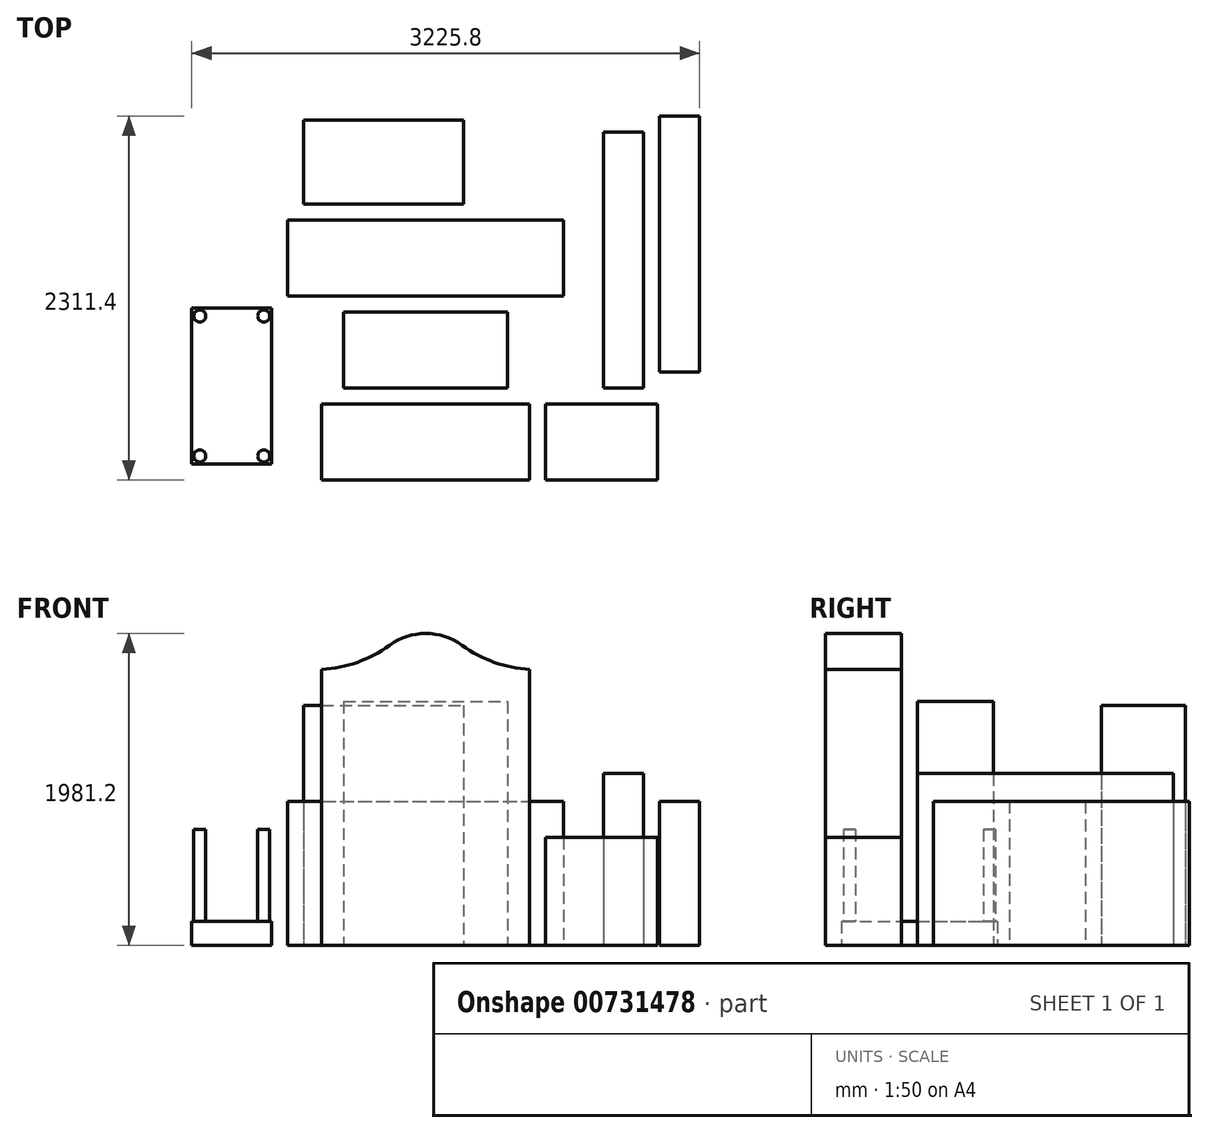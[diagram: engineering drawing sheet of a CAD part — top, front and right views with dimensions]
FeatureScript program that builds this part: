
annotation { "Feature Type Name" : "Feature", "Feature Type Description" : "" }
export const myFeature = defineFeature(function(context is Context, id is Id, definition is map)
    precondition{}
    {
        {
            var Q0;
            Q0=qCreatedBy(makeId("Top.planeOp"),FACE);
            var sketch = newSketch(context, id + "F0", { "sketchPlane" : qUnion([Q0])});
            skLineSegment(sketch, "E0.bottom", {"start": v(-876.3, 482.6) * mm, "end": v(876.3, 482.6) * mm});
            skLineSegment(sketch, "E0.top", {"start": v(-876.3, 0) * mm, "end": v(876.3, 0) * mm});
            skLineSegment(sketch, "E0.left", {"start": v(-876.3, 482.6) * mm, "end": v(-876.3, 0) * mm});
            skLineSegment(sketch, "E0.right", {"start": v(876.3, 482.6) * mm, "end": v(876.3, 0) * mm});
            skLineSegment(sketch, "E1.bottom", {"start": v(-520.7, -101.6) * mm, "end": v(520.7, -101.6) * mm});
            skLineSegment(sketch, "E1.top", {"start": v(-520.7, -584.2) * mm, "end": v(520.7, -584.2) * mm});
            skLineSegment(sketch, "E1.left", {"start": v(-520.7, -101.6) * mm, "end": v(-520.7, -584.2) * mm});
            skLineSegment(sketch, "E1.right", {"start": v(520.7, -101.6) * mm, "end": v(520.7, -584.2) * mm});
            skLineSegment(sketch, "E2.bottom", {"start": v(-660.4, -685.8) * mm, "end": v(660.4, -685.8) * mm});
            skLineSegment(sketch, "E2.top", {"start": v(-660.4, -1168.4) * mm, "end": v(660.4, -1168.4) * mm});
            skLineSegment(sketch, "E2.left", {"start": v(-660.4, -685.8) * mm, "end": v(-660.4, -1168.4) * mm});
            skLineSegment(sketch, "E2.right", {"start": v(660.4, -685.8) * mm, "end": v(660.4, -1168.4) * mm});
            skLineSegment(sketch, "E3", {"start": v(0, -101.6) * mm, "end": v(0, 0) * mm});
            skLineSegment(sketch, "E4", {"start": v(0, -584.2) * mm, "end": v(0, -685.8) * mm});
            skLineSegment(sketch, "E5.bottom", {"start": v(-774.7, 584.2) * mm, "end": v(241.3, 584.2) * mm});
            skLineSegment(sketch, "E5.top", {"start": v(-774.7, 1117.6) * mm, "end": v(241.3, 1117.6) * mm});
            skLineSegment(sketch, "E5.left", {"start": v(-774.7, 584.2) * mm, "end": v(-774.7, 1117.6) * mm});
            skLineSegment(sketch, "E5.right", {"start": v(241.3, 584.2) * mm, "end": v(241.3, 1117.6) * mm});
            skLineSegment(sketch, "E6.bottom", {"start": v(762, -1168.4) * mm, "end": v(1473.2, -1168.4) * mm});
            skLineSegment(sketch, "E6.top", {"start": v(762, -685.8) * mm, "end": v(1473.2, -685.8) * mm});
            skLineSegment(sketch, "E6.left", {"start": v(762, -1168.4) * mm, "end": v(762, -685.8) * mm});
            skLineSegment(sketch, "E6.right", {"start": v(1473.2, -1168.4) * mm, "end": v(1473.2, -685.8) * mm});
            skLineSegment(sketch, "E7.bottom", {"start": v(1130.3, -584.2) * mm, "end": v(1384.3, -584.2) * mm});
            skLineSegment(sketch, "E7.top", {"start": v(1130.3, 1041.4) * mm, "end": v(1384.3, 1041.4) * mm});
            skLineSegment(sketch, "E7.left", {"start": v(1130.3, -584.2) * mm, "end": v(1130.3, 1041.4) * mm});
            skLineSegment(sketch, "E7.right", {"start": v(1384.3, -584.2) * mm, "end": v(1384.3, 1041.4) * mm});
            skLineSegment(sketch, "E8.bottom", {"start": v(1485.9, 1143) * mm, "end": v(1739.9, 1143) * mm});
            skLineSegment(sketch, "E8.top", {"start": v(1485.9, -482.6) * mm, "end": v(1739.9, -482.6) * mm});
            skLineSegment(sketch, "E8.left", {"start": v(1485.9, 1143) * mm, "end": v(1485.9, -482.6) * mm});
            skLineSegment(sketch, "E8.right", {"start": v(1739.9, 1143) * mm, "end": v(1739.9, -482.6) * mm});
            skLineSegment(sketch, "E9.bottom", {"start": v(-977.9, -1066.8) * mm, "end": v(-1485.9, -1066.8) * mm});
            skLineSegment(sketch, "E9.top", {"start": v(-977.9, -76.2) * mm, "end": v(-1485.9, -76.2) * mm});
            skLineSegment(sketch, "E9.left", {"start": v(-977.9, -1066.8) * mm, "end": v(-977.9, -76.2) * mm});
            skLineSegment(sketch, "E9.right", {"start": v(-1485.9, -1066.8) * mm, "end": v(-1485.9, -76.2) * mm});
            skLineSegment(sketch, "E10.0", {"start": v(-1028.7, -127) * mm, "end": v(-1435.1, -127) * mm});
            skLineSegment(sketch, "E10.1", {"start": v(-1028.7, -1016) * mm, "end": v(-1028.7, -127) * mm, "construction": true});
            skLineSegment(sketch, "E10.2", {"start": v(-1028.7, -1016) * mm, "end": v(-1435.1, -1016) * mm});
            skLineSegment(sketch, "E10.3", {"start": v(-1435.1, -1016) * mm, "end": v(-1435.1, -127) * mm, "construction": true});
            skCircle(sketch, "E11", {"center": v(-1435.1, -127) * mm, "radius": 38.1 * mm});
            skCircle(sketch, "E12", {"center": v(-1028.7, -127) * mm, "radius": 38.1 * mm});
            skCircle(sketch, "E13", {"center": v(-1028.7, -1016) * mm, "radius": 38.1 * mm});
            skCircle(sketch, "E14", {"center": v(-1435.1, -1016) * mm, "radius": 38.1 * mm});
            skSolve(sketch);
        }
        {
            var Q0;
            Q0=makeQuery(id+"F0.imprint","IMPRINT",FACE,{"disambiguationData":[TD([[makeQuery(id+"F0.imprint","IMPRINT",EDGE,{"derivedFrom":sQuery(id+"F0.wireOp",EDGE,"E0.bottom")}),-1.0]])]});
            extrude(context, id + "F1", {"entities" : qUnion([Q0]), "depth" : 914.4 * mm, "offsetDistance" : 25.4 * mm});
        }
        {
            var Q0;
            {var subQ3=sQuery(id+"F0.wireOp",EDGE,"E1.left");Q0=makeQuery(id+"F0.imprint","IMPRINT",FACE,{"disambiguationData":[TD([[makeQuery(id+"F0.imprint","IMPRINT",EDGE,{"derivedFrom":subQ3}),1.0]])]});}
            extrude(context, id + "F2", {"entities" : qUnion([Q0]), "depth" : 1549.4 * mm, "offsetDistance" : 25.4 * mm});
        }
        {
            var Q0;
            Q0=makeQuery(id+"F0.imprint","IMPRINT",FACE,{"disambiguationData":[TD([[makeQuery(id+"F0.imprint","IMPRINT",EDGE,{"derivedFrom":sQuery(id+"F0.wireOp",EDGE,"E2.top")}),1.0]])]});
            extrude(context, id + "F3", {"entities" : qUnion([Q0]), "depth" : 1752.6 * mm, "offsetDistance" : 25.4 * mm});
        }
        {
            var Q0;
            Q0=makeQuery(id+"F3.opExtrude","SWEPT_FACE",FACE,{"disambiguationData":[OSD([sQuery(id+"F0.wireOp",EDGE,"E2.top")])]});
            var sketch = newSketch(context, id + "F4", { "sketchPlane" : qUnion([Q0])});
            skArc(sketch, "E15", {"start": v(-660.4, 1752.6) * mm, "mid": v(-434.61, 1798.39) * mm, "end": v(-230.93, 1906.04) * mm});
            skArc(sketch, "E16", {"start": v(230.93, 1906.04) * mm, "mid": v(0, 1981.2) * mm, "end": v(-230.93, 1906.04) * mm});
            skArc(sketch, "E17", {"start": v(230.93, 1906.04) * mm, "mid": v(434.61, 1798.39) * mm, "end": v(660.4, 1752.6) * mm});
            skLineSegment(sketch, "E18", {"start": v(0, 1752.6) * mm, "end": v(0, 1981.2) * mm});
            skSolve(sketch);
        }
        {
            var Q0;
            {var subQ0=sQuery(id+"F4.wireOp",EDGE,"E15");Q0=makeQuery(id+"F4.imprint","IMPRINT",FACE,{"disambiguationData":[TD([[makeQuery(id+"F4.imprint","IMPRINT",EDGE,{"derivedFrom":subQ0}),-1.0]])]});}
            var Q1;
            {var subQ0=sQuery(id+"F4.wireOp",EDGE,"E17");Q1=makeQuery(id+"F4.imprint","IMPRINT",FACE,{"disambiguationData":[TD([[makeQuery(id+"F4.imprint","IMPRINT",EDGE,{"derivedFrom":subQ0}),-1.0]])]});}
            var Q2;
            Q2=makeQuery(id+"F3.opExtrude","SWEPT_FACE",FACE,{"disambiguationData":[OSD([sQuery(id+"F0.wireOp",EDGE,"E2.bottom")])]});
            extrude(context, id + "F5", {"entities" : qUnion([Q0, Q1]), "operationType" : NewBodyOperationType.ADD, "endBound" : BoundingType.UP_TO_SURFACE, "oppositeDirection" : true, "depth" : 25.4 * mm, "endBoundEntityFace" : qUnion([Q2]), "offsetDistance" : 25.4 * mm});
        }
        {
            var Q0;
            Q0=makeQuery(id+"F0.imprint","IMPRINT",FACE,{"disambiguationData":[TD([[makeQuery(id+"F0.imprint","IMPRINT",EDGE,{"derivedFrom":sQuery(id+"F0.wireOp",EDGE,"E5.bottom")}),1.0]])]});
            extrude(context, id + "F6", {"entities" : qUnion([Q0]), "depth" : 1524 * mm, "offsetDistance" : 25.4 * mm});
        }
        {
            var Q0;
            Q0=makeQuery(id+"F0.imprint","IMPRINT",FACE,{"disambiguationData":[TD([[makeQuery(id+"F0.imprint","IMPRINT",EDGE,{"derivedFrom":sQuery(id+"F0.wireOp",EDGE,"E6.bottom")}),1.0]])]});
            extrude(context, id + "F7", {"entities" : qUnion([Q0]), "depth" : 685.8 * mm, "offsetDistance" : 25.4 * mm});
        }
        {
            var Q0;
            Q0=makeQuery(id+"F0.imprint","IMPRINT",FACE,{"disambiguationData":[TD([[makeQuery(id+"F0.imprint","IMPRINT",EDGE,{"derivedFrom":sQuery(id+"F0.wireOp",EDGE,"E7.bottom")}),1.0]])]});
            extrude(context, id + "F8", {"entities" : qUnion([Q0]), "depth" : 1092.2 * mm, "offsetDistance" : 25.4 * mm});
        }
        {
            var Q0;
            Q0=makeQuery(id+"F0.imprint","IMPRINT",FACE,{"disambiguationData":[TD([[makeQuery(id+"F0.imprint","IMPRINT",EDGE,{"derivedFrom":sQuery(id+"F0.wireOp",EDGE,"E8.bottom")}),-1.0]])]});
            extrude(context, id + "F9", {"entities" : qUnion([Q0]), "depth" : 914.4 * mm, "offsetDistance" : 25.4 * mm});
        }
        {
            var Q0;
            Q0=makeQuery(id+"F0.imprint","IMPRINT",FACE,{"disambiguationData":[TD([[makeQuery(id+"F0.imprint","IMPRINT",EDGE,{"derivedFrom":sQuery(id+"F0.wireOp",EDGE,"E9.bottom")}),-1.0]])]});
            extrude(context, id + "F10", {"entities" : qUnion([Q0]), "depth" : 152.4 * mm, "offsetDistance" : 25.4 * mm});
        }
        {
            var Q0;
            Q0=makeQuery(id+"F0.imprint","IMPRINT",FACE,{"disambiguationData":[TD([[makeQuery(id+"F0.imprint","IMPRINT",EDGE,{"derivedFrom":sQuery(id+"F0.wireOp",EDGE,"E11")}),1.0]])]});
            var Q1;
            Q1=makeQuery(id+"F0.imprint","IMPRINT",FACE,{"disambiguationData":[TD([[makeQuery(id+"F0.imprint","IMPRINT",EDGE,{"derivedFrom":sQuery(id+"F0.wireOp",EDGE,"E12")}),1.0]])]});
            var Q2;
            Q2=makeQuery(id+"F0.imprint","IMPRINT",FACE,{"disambiguationData":[TD([[makeQuery(id+"F0.imprint","IMPRINT",EDGE,{"derivedFrom":sQuery(id+"F0.wireOp",EDGE,"E13")}),1.0]])]});
            var Q3;
            Q3=makeQuery(id+"F0.imprint","IMPRINT",FACE,{"disambiguationData":[TD([[makeQuery(id+"F0.imprint","IMPRINT",EDGE,{"derivedFrom":sQuery(id+"F0.wireOp",EDGE,"E14")}),1.0]])]});
            extrude(context, id + "F11", {"entities" : qUnion([Q0, Q1, Q2, Q3]), "operationType" : NewBodyOperationType.ADD, "depth" : 736.6 * mm, "offsetDistance" : 25.4 * mm});
        }
    });
